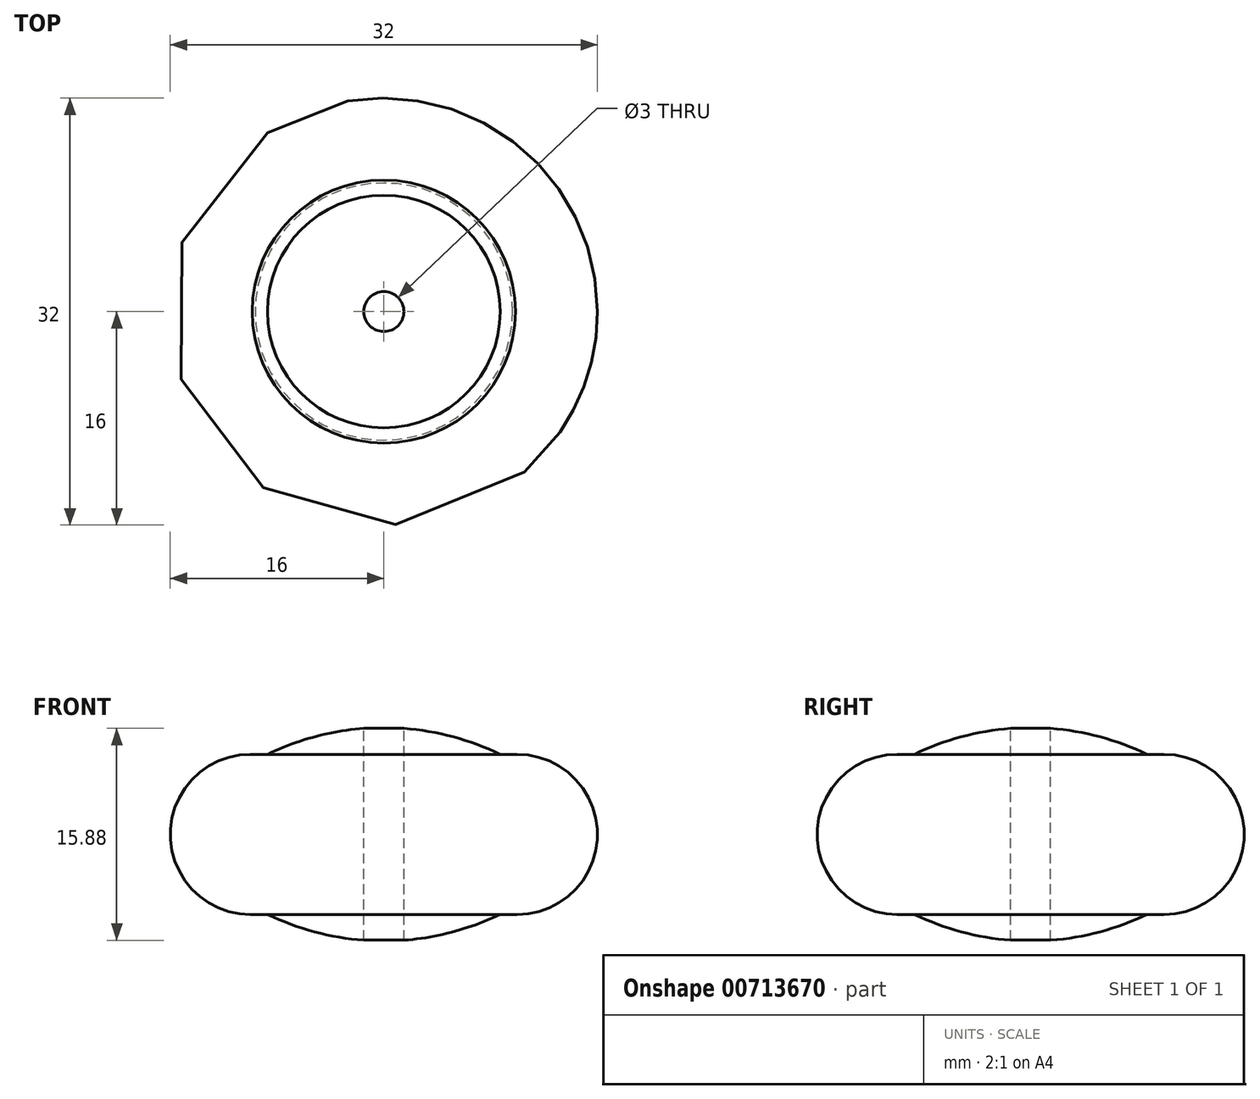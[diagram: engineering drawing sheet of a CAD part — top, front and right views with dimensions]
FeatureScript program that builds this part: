
annotation { "Feature Type Name" : "Feature", "Feature Type Description" : "" }
export const myFeature = defineFeature(function(context is Context, id is Id, definition is map)
    precondition{}
    {
        {
            var Q0;
            Q0=qCreatedBy(makeId("Front.planeOp"),FACE);
            var sketch = newSketch(context, id + "F0", { "sketchPlane" : qUnion([Q0])});
            skArc(sketch, "E0", {"start": v(-8.72, -5.99) * mm, "mid": v(-4.48, -7.48) * mm, "end": v(0, -8) * mm});
            skLineSegment(sketch, "E1", {"start": v(0, 0) * mm, "end": v(1105.39, 0) * mm, "construction": true});
            skLineSegment(sketch, "E2", {"start": v(0, 0) * mm, "end": v(0, 946.63) * mm, "construction": true});
            skArc(sketch, "E3", {"start": v(-9.86, 6) * mm, "mid": v(-16, -0.11) * mm, "end": v(-9.63, -5.99) * mm});
            skLineSegment(sketch, "E4", {"start": v(-9.86, 6) * mm, "end": v(-8.72, 6) * mm});
            skLineSegment(sketch, "E5", {"start": v(-10.37, -5.99) * mm, "end": v(-8.72, -5.99) * mm});
            skArc(sketch, "E6.trimOffspring", {"start": v(0, 8) * mm, "mid": v(-4.47, 7.5) * mm, "end": v(-8.72, 6) * mm});
            skLineSegment(sketch, "E7", {"start": v(0, 8) * mm, "end": v(0, -8) * mm});
            skSolve(sketch);
        }
        {
            var Q0;
            Q0=qSketchRegion(id+"F0",true);
            var Q1;
            Q1=sQuery(id+"F0.wireOp",EDGE,"E7");
            revolve(context, id + "F1", {"surfaceOperationType" : NewSurfaceOperationType.NEW, "entities" : qUnion([Q0]), "axis" : qUnion([Q1]), "revolveType" : RevolveType.FULL});
        }
        {
            var Q0;
            Q0=qCreatedBy(makeId("Top.planeOp"),FACE);
            var sketch = newSketch(context, id + "F2", { "sketchPlane" : qUnion([Q0])});
            skCircle(sketch, "E8", {"center": v(0, 0) * mm, "radius": 1.5 * mm});
            skSolve(sketch);
        }
        {
            var Q0;
            Q0=qSketchRegion(id+"F2",true);
            extrude(context, id + "F3", {"entities" : qUnion([Q0]), "operationType" : NewBodyOperationType.REMOVE, "endBound" : BoundingType.THROUGH_ALL, "oppositeDirection" : true, "depth" : 25.4 * mm, "offsetDistance" : 25.4 * mm, "hasSecondDirection" : true, "secondDirectionBound" : SecondDirectionBoundingType.THROUGH_ALL, "secondDirectionOppositeDirection" : false, "secondDirectionDepth" : 25.4 * mm});
        }
    });
